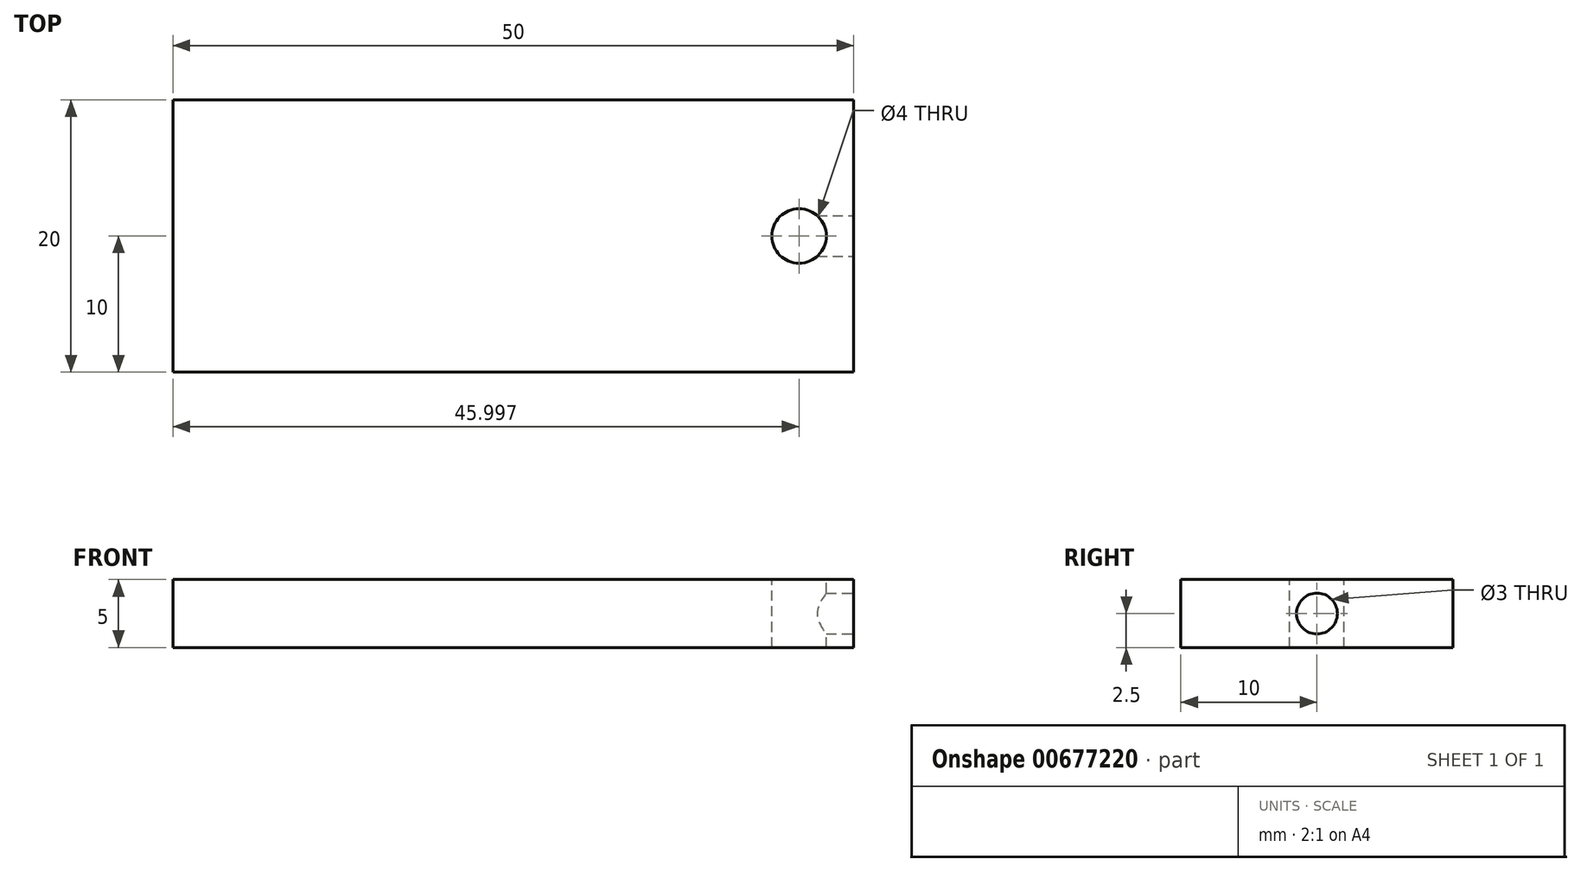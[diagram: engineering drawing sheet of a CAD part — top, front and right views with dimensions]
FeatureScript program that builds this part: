
annotation { "Feature Type Name" : "Feature", "Feature Type Description" : "" }
export const myFeature = defineFeature(function(context is Context, id is Id, definition is map)
    precondition{}
    {
        {
            var Q0;
            Q0=qCreatedBy(makeId("Top.planeOp"),FACE);
            var sketch = newSketch(context, id + "F0", { "sketchPlane" : qUnion([Q0])});
            skLineSegment(sketch, "E0.bottom", {"start": v(26.9, -10) * mm, "end": v(-23.1, -10) * mm});
            skLineSegment(sketch, "E0.top", {"start": v(26.9, 10) * mm, "end": v(-23.1, 10) * mm});
            skLineSegment(sketch, "E0.left", {"start": v(26.9, -10) * mm, "end": v(26.9, 10) * mm});
            skLineSegment(sketch, "E0.right", {"start": v(-23.1, -10) * mm, "end": v(-23.1, 10) * mm});
            skPoint(sketch, "E0.middle", {"position": v(1.9, 0) * mm});
            skSolve(sketch);
        }
        {
            var Q0;
            Q0 = qSketchRegion(id + "F0", true);
            extrude(context, id + "F1", {"entities" : qUnion([Q0]), "endBound" : BoundingType.SYMMETRIC, "depth" : 5 * mm, "offsetDistance" : 25 * mm});
        }
        {
            var Q0;
            Q0=makeQuery(id+"F1.opExtrude","CAP_FACE",FACE,{"disambiguationData":[OSD([sQuery(id+"F0.wireOp",EDGE,"E0.bottom"),sQuery(id+"F0.wireOp",EDGE,"E0.top"),sQuery(id+"F0.wireOp",EDGE,"E0.left"),sQuery(id+"F0.wireOp",EDGE,"E0.right")])],"isStart":false});
            var sketch = newSketch(context, id + "F2", { "sketchPlane" : qUnion([Q0])});
            skCircle(sketch, "E1", {"center": v(22.9, 0) * mm, "radius": 2 * mm});
            skSolve(sketch);
        }
        {
            var Q0;
            Q0 = qSketchRegion(id + "F2", true);
            extrude(context, id + "F3", {"entities" : qUnion([Q0]), "operationType" : NewBodyOperationType.REMOVE, "endBound" : BoundingType.THROUGH_ALL, "oppositeDirection" : true, "depth" : 25 * mm, "offsetDistance" : 25 * mm});
        }
        {
            var Q0;
            Q0=makeQuery(id+"F1.opExtrude","SWEPT_FACE",FACE,{"disambiguationData":[OSD([sQuery(id+"F0.wireOp",EDGE,"E0.left")])]});
            var sketch = newSketch(context, id + "F4", { "sketchPlane" : qUnion([Q0])});
            skCircle(sketch, "E2", {"center": v(0, 0) * mm, "radius": 1.5 * mm});
            skSolve(sketch);
        }
        {
            var Q0;
            Q0 = qSketchRegion(id + "F4", true);
            extrude(context, id + "F5", {"entities" : qUnion([Q0]), "operationType" : NewBodyOperationType.REMOVE, "oppositeDirection" : true, "depth" : 5 * mm, "offsetDistance" : 25 * mm});
        }
    });
